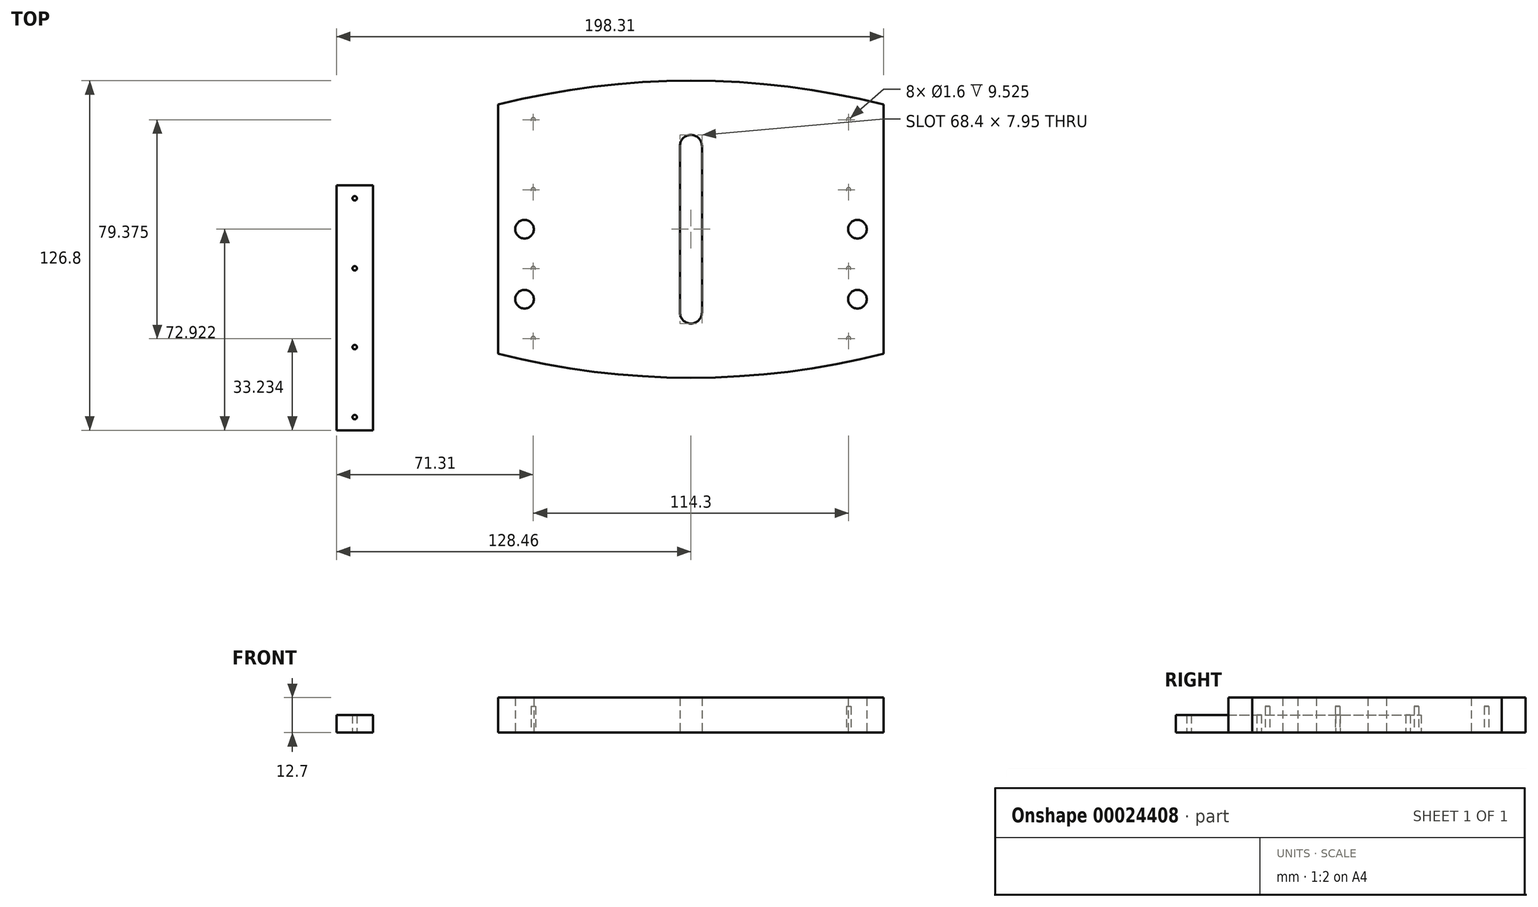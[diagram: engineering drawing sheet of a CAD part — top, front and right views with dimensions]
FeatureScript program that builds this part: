
annotation { "Feature Type Name" : "Feature", "Feature Type Description" : "" }
export const myFeature = defineFeature(function(context is Context, id is Id, definition is map)
    precondition{}
    {
        {
            var Q0;
            Q0=qCreatedBy(makeId("Top.planeOp"),FACE);
            var sketch = newSketch(context, id + "F0", { "sketchPlane" : qUnion([Q0])});
            skLineSegment(sketch, "E0.bottom", {"start": v(0, 0) * mm, "end": v(139.7, 0) * mm, "construction": true});
            skLineSegment(sketch, "E0.top", {"start": v(0, 45.21) * mm, "end": v(139.7, 45.21) * mm, "construction": true});
            skLineSegment(sketch, "E0.left", {"start": v(0, 0) * mm, "end": v(0, 45.21) * mm});
            skLineSegment(sketch, "E0.right", {"start": v(139.7, 0) * mm, "end": v(139.7, 45.21) * mm});
            skLineSegment(sketch, "E1", {"start": v(0, 45.21) * mm, "end": v(0, 90.42) * mm});
            skLineSegment(sketch, "E2", {"start": v(0, 90.42) * mm, "end": v(139.7, 90.42) * mm, "construction": true});
            skLineSegment(sketch, "E3", {"start": v(139.7, 90.42) * mm, "end": v(139.7, 45.21) * mm});
            skCircle(sketch, "E4", {"center": v(9.52, 45.21) * mm, "radius": 3.37 * mm});
            skCircle(sketch, "E5", {"center": v(9.53, 19.81) * mm, "radius": 3.37 * mm});
            skCircle(sketch, "E6", {"center": v(130.18, 19.81) * mm, "radius": 3.37 * mm});
            skCircle(sketch, "E7", {"center": v(130.18, 45.21) * mm, "radius": 3.37 * mm});
            skArc(sketch, "E8", {"start": v(139.7, 90.42) * mm, "mid": v(69.85, 99.1) * mm, "end": v(0, 90.42) * mm});
            skArc(sketch, "E9", {"start": v(0, 0) * mm, "mid": v(69.85, -8.67) * mm, "end": v(139.7, 0) * mm});
            skLineSegment(sketch, "E10", {"start": v(69.85, 45.21) * mm, "end": v(69.85, 75.44) * mm, "construction": true});
            skCircle(sketch, "E11", {"center": v(69.85, 75.44) * mm, "radius": 3.98 * mm});
            skLineSegment(sketch, "E12", {"start": v(69.85, 45.21) * mm, "end": v(69.85, 14.99) * mm, "construction": true});
            skCircle(sketch, "E13", {"center": v(69.85, 14.99) * mm, "radius": 3.98 * mm});
            skLineSegment(sketch, "E14", {"start": v(65.87, 75.44) * mm, "end": v(65.87, 14.99) * mm});
            skLineSegment(sketch, "E15", {"start": v(73.83, 14.99) * mm, "end": v(73.83, 75.44) * mm});
            skSolve(sketch);
        }
        {
            var Q0;
            Q0=makeQuery(id+"F0.imprint","IMPRINT",FACE,{"disambiguationData":[TD([[makeQuery(id+"F0.imprint","IMPRINT",EDGE,{"derivedFrom":sQuery(id+"F0.wireOp",EDGE,"E0.left")}),-1.0]])]});
            extrude(context, id + "F1", {"entities" : qUnion([Q0]), "depth" : 12.7 * mm});
        }
        {
            var Q0;
            Q0=makeQuery(id+"F1.opExtrude","CAP_FACE",FACE,{"disambiguationData":[OSD([sQuery(id+"F0.wireOp",EDGE,"E0.left"),sQuery(id+"F0.wireOp",EDGE,"E0.right"),sQuery(id+"F0.wireOp",EDGE,"E1"),sQuery(id+"F0.wireOp",EDGE,"E3"),sQuery(id+"F0.wireOp",EDGE,"E4"),sQuery(id+"F0.wireOp",EDGE,"E5"),sQuery(id+"F0.wireOp",EDGE,"E6"),sQuery(id+"F0.wireOp",EDGE,"E7"),sQuery(id+"F0.wireOp",EDGE,"E8"),sQuery(id+"F0.wireOp",EDGE,"E9"),sQuery(id+"F0.wireOp",EDGE,"E11"),sQuery(id+"F0.wireOp",EDGE,"E13"),sQuery(id+"F0.wireOp",EDGE,"E14"),sQuery(id+"F0.wireOp",EDGE,"E15")])],"isStart":true});
            var sketch = newSketch(context, id + "F2", { "sketchPlane" : qUnion([Q0])});
            skLineSegment(sketch, "E16", {"start": v(12.7, 2.9) * mm, "end": v(12.7, -45.21) * mm, "construction": true});
            skLineSegment(sketch, "E17", {"start": v(127, 2.9) * mm, "end": v(127, -45.21) * mm, "construction": true});
            skLineSegment(sketch, "E18", {"start": v(0, -45.21) * mm, "end": v(139.7, -45.21) * mm, "construction": true});
            skLineSegment(sketch, "E19", {"start": v(12.7, -45.21) * mm, "end": v(12.7, -93.32) * mm, "construction": true});
            skLineSegment(sketch, "E20", {"start": v(127, -45.21) * mm, "end": v(127, -93.32) * mm, "construction": true});
            skCircle(sketch, "E21", {"center": v(12.7, -5.52) * mm, "radius": 0.8 * mm});
            skCircle(sketch, "E22", {"center": v(12.7, -30.92) * mm, "radius": 0.8 * mm});
            skCircle(sketch, "E23", {"center": v(12.7, -59.5) * mm, "radius": 0.8 * mm});
            skCircle(sketch, "E24", {"center": v(12.7, -84.9) * mm, "radius": 0.8 * mm});
            skCircle(sketch, "E25", {"center": v(127, -5.52) * mm, "radius": 0.8 * mm});
            skCircle(sketch, "E26", {"center": v(127, -30.92) * mm, "radius": 0.8 * mm});
            skCircle(sketch, "E27", {"center": v(127, -59.5) * mm, "radius": 0.8 * mm});
            skCircle(sketch, "E28", {"center": v(127, -84.9) * mm, "radius": 0.8 * mm});
            skSolve(sketch);
        }
        {
            var Q0;
            Q0 = qSketchRegion(id + "F2", true);
            extrude(context, id + "F3", {"entities" : qUnion([Q0]), "operationType" : NewBodyOperationType.REMOVE, "oppositeDirection" : true, "depth" : 9.52 * mm});
        }
        {
            var Q0;
            Q0=qCreatedBy(makeId("Top.planeOp"),FACE);
            var sketch = newSketch(context, id + "F4", { "sketchPlane" : qUnion([Q0])});
            skLineSegment(sketch, "E29", {"start": v(-52, 16.74) * mm, "end": v(-52, -27.71) * mm, "construction": true});
            skLineSegment(sketch, "E30", {"start": v(-52, 61.19) * mm, "end": v(-52, 16.74) * mm, "construction": true});
            skCircle(sketch, "E31", {"center": v(-52, 2.45) * mm, "radius": 0.8 * mm});
            skCircle(sketch, "E32", {"center": v(-52, -22.95) * mm, "radius": 0.8 * mm});
            skCircle(sketch, "E33", {"center": v(-52, 31.03) * mm, "radius": 0.8 * mm});
            skCircle(sketch, "E34", {"center": v(-52, 56.43) * mm, "radius": 0.8 * mm});
            skLineSegment(sketch, "E35.bottom", {"start": v(-58.61, -27.71) * mm, "end": v(-45.4, -27.71) * mm});
            skLineSegment(sketch, "E35.top", {"start": v(-58.61, 61.19) * mm, "end": v(-45.4, 61.19) * mm});
            skLineSegment(sketch, "E35.left", {"start": v(-58.61, -27.71) * mm, "end": v(-58.61, 61.19) * mm});
            skLineSegment(sketch, "E35.right", {"start": v(-45.4, -27.71) * mm, "end": v(-45.4, 61.19) * mm});
            skSolve(sketch);
        }
        {
            var Q0;
            Q0 = qSketchRegion(id + "F4", true);
            extrude(context, id + "F5", {"entities" : qUnion([Q0]), "depth" : 6.35 * mm});
        }
    });
